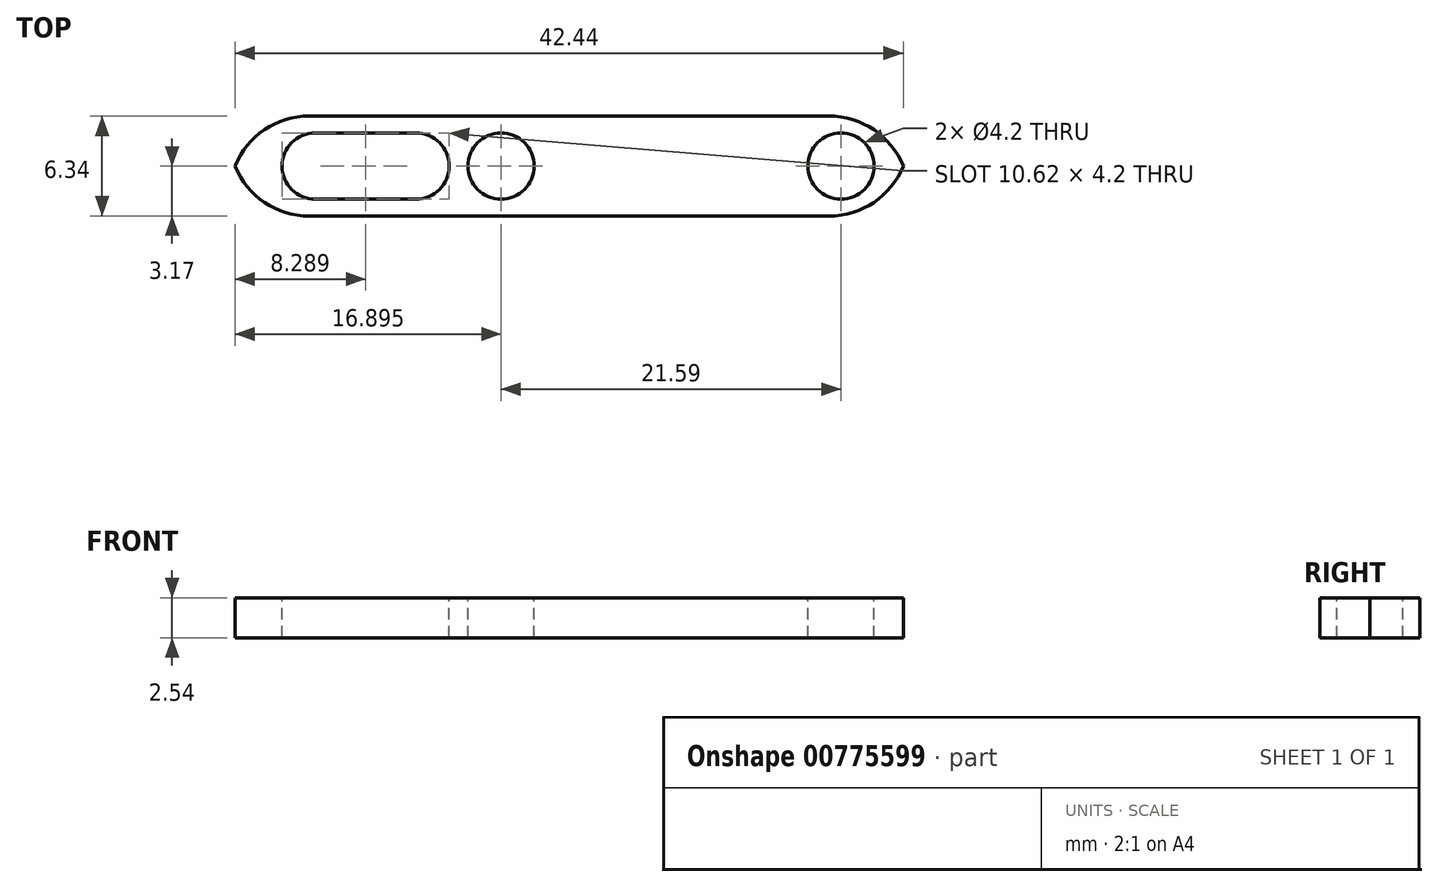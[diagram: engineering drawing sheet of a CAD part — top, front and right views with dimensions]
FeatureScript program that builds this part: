
annotation { "Feature Type Name" : "Feature", "Feature Type Description" : "" }
export const myFeature = defineFeature(function(context is Context, id is Id, definition is map)
    precondition{}
    {
        {
            var Q0;
            Q0=qCreatedBy(makeId("Top.planeOp"),FACE);
            var sketch = newSketch(context, id + "F0", { "sketchPlane" : qUnion([Q0])});
            skLineSegment(sketch, "E0.bottom", {"start": v(21.59, 3.17) * mm, "end": v(-21.59, 3.17) * mm});
            skLineSegment(sketch, "E0.top", {"start": v(21.59, -3.18) * mm, "end": v(-21.59, -3.18) * mm});
            skLineSegment(sketch, "E0.left", {"start": v(21.59, 3.17) * mm, "end": v(21.59, -3.18) * mm});
            skLineSegment(sketch, "E0.right", {"start": v(-21.59, 3.17) * mm, "end": v(-21.59, -3.18) * mm});
            skPoint(sketch, "E0.middle", {"position": v(0, 0) * mm});
            skSolve(sketch);
        }
        {
            var Q0;
            Q0 = qSketchRegion(id + "F0", true);
            extrude(context, id + "F1", {"entities" : qUnion([Q0]), "depth" : 2.54 * mm, "offsetDistance" : 25.4 * mm});
        }
        {
            var Q0;
            Q0=makeQuery(id+"F1.opExtrude","SWEPT_EDGE",EDGE,{"disambiguationData":[OSD([sQuery(id+"F0.wireOp",EDGE,"E0.top"),sQuery(id+"F0.wireOp",EDGE,"E0.left")])]});
            var Q1;
            Q1=makeQuery(id+"F1.opExtrude","SWEPT_EDGE",EDGE,{"disambiguationData":[OSD([sQuery(id+"F0.wireOp",EDGE,"E0.bottom"),sQuery(id+"F0.wireOp",EDGE,"E0.left")])]});
            var Q2;
            Q2=makeQuery(id+"F1.opExtrude","SWEPT_EDGE",EDGE,{"disambiguationData":[OSD([sQuery(id+"F0.wireOp",EDGE,"E0.bottom"),sQuery(id+"F0.wireOp",EDGE,"E0.right")])]});
            var Q3;
            Q3=makeQuery(id+"F1.opExtrude","SWEPT_EDGE",EDGE,{"disambiguationData":[OSD([sQuery(id+"F0.wireOp",EDGE,"E0.top"),sQuery(id+"F0.wireOp",EDGE,"E0.right")])]});
            fillet(context, id + "F2", {"entities" : qUnion([Q0, Q1, Q2, Q3]), "radius" : 5.08 * mm, "tangentPropagation" : true, "allowEdgeOverflow" : false});
        }
        {
            var Q0;
            Q0=makeQuery(id+"F1.opExtrude","CAP_FACE",FACE,{"disambiguationData":[OSD([sQuery(id+"F0.wireOp",EDGE,"E0.bottom"),sQuery(id+"F0.wireOp",EDGE,"E0.top"),sQuery(id+"F0.wireOp",EDGE,"E0.left"),sQuery(id+"F0.wireOp",EDGE,"E0.right")])],"isStart":false});
            var sketch = newSketch(context, id + "F3", { "sketchPlane" : qUnion([Q0])});
            skCircle(sketch, "E1", {"center": v(17.26, 0) * mm, "radius": 2.1 * mm});
            skCircle(sketch, "E2", {"center": v(-4.33, 0) * mm, "radius": 2.1 * mm});
            skArc(sketch, "E3", {"start": v(-16.14, 2.1) * mm, "mid": v(-18.24, 0) * mm, "end": v(-16.14, -2.1) * mm});
            skArc(sketch, "E4", {"start": v(-9.72, -2.1) * mm, "mid": v(-7.62, 0) * mm, "end": v(-9.72, 2.1) * mm});
            skLineSegment(sketch, "E5", {"start": v(-16.14, 2.1) * mm, "end": v(-9.72, 2.1) * mm});
            skLineSegment(sketch, "E6", {"start": v(-16.14, -2.1) * mm, "end": v(-9.72, -2.1) * mm});
            skLineSegment(sketch, "E7", {"start": v(-21.22, 0) * mm, "end": v(21.22, 0) * mm});
            skSolve(sketch);
        }
        {
            var Q0;
            Q0 = qSketchRegion(id + "F3", true);
            extrude(context, id + "F4", {"entities" : qUnion([Q0]), "operationType" : NewBodyOperationType.REMOVE, "endBound" : BoundingType.THROUGH_ALL, "oppositeDirection" : true, "depth" : 25.4 * mm, "offsetDistance" : 25.4 * mm});
        }
    });
